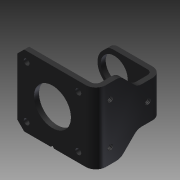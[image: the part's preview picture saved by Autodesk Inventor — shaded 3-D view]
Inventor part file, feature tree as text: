
AUTODESK INVENTOR PART (.ipt)
format: ipt  version: 2015 (Build 190159000, 159)  size: 282,624 bytes
history: native  units: mm
features: extrude x6, hole x3, fillet x3, chamfer x2, plane x1, other x1
ambient origin geometry x8: Origin, YZ Plane, XZ Plane, XY Plane, X Axis, Y Axis, Z Axis, Center Point
bodies: Solid1 (feature_tree)
feature tree (16):
  extrude  "Extrusión1"  Depth=3.0mm
  hole  "Agujero1"  [1 undecoded]
  hole  "Agujero2"  [1 undecoded]
  extrude  "Extrusión2"  Depth=3.0mm
  fillet  "Empalme1"  Radius=22.15mm
  chamfer  "Chaflán1"  Distance=31.0mm
  plane  "Plano de trabajo1"
  hole  "Agujero3"  [1 undecoded]
  extrude  "Extrusión5"  Depth=6.0mm
  extrude  "Extrusión6"  Depth=4.0mm TaperAngle=45.0deg
  fillet  "Redondeo de esquina1"  Radius=3.0mm
  extrude  "Extrusión7"  Depth=40.0mm
  chamfer  "Chaflán de esquina1"  Distance=10.0mm
  fillet  "Redondeo de esquina2"  Radius=25.0mm
  extrude  "Extrusión8"  Depth=22.5mm
  other  "Definición1"
note: 3 required parameter values undecoded (feature->parameter linkage not recoverable at this tier; creation-order binding heuristic only, values carry confidence <= 0.55)
